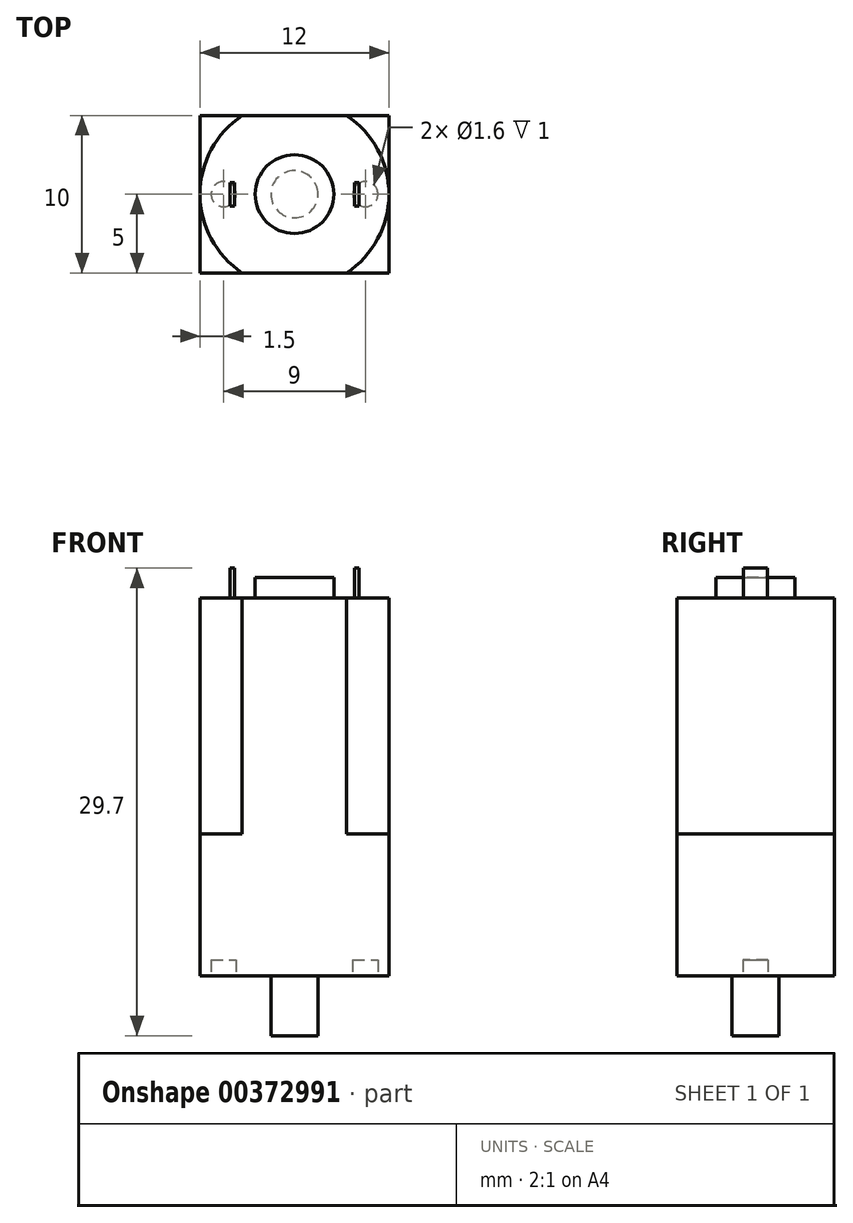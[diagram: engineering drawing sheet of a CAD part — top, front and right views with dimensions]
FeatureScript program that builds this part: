
annotation { "Feature Type Name" : "Feature", "Feature Type Description" : "" }
export const myFeature = defineFeature(function(context is Context, id is Id, definition is map)
    precondition{}
    {
        {
            var Q0;
            Q0=qCreatedBy(makeId("Top.planeOp"),FACE);
            var sketch = newSketch(context, id + "F0", { "sketchPlane" : qUnion([Q0])});
            skArc(sketch, "E0", {"start": v(-3.32, 5) * mm, "mid": v(-6, 0) * mm, "end": v(-3.32, -5) * mm});
            skLineSegment(sketch, "E1", {"start": v(-6, 0) * mm, "end": v(6, 0) * mm, "construction": true});
            skLineSegment(sketch, "E2", {"start": v(-3.32, 5) * mm, "end": v(3.32, 5) * mm});
            skLineSegment(sketch, "E3", {"start": v(-3.32, -5) * mm, "end": v(3.32, -5) * mm});
            skArc(sketch, "E4.trimOffspring", {"start": v(3.32, -5) * mm, "mid": v(6, 0) * mm, "end": v(3.32, 5) * mm});
            skSolve(sketch);
        }
        {
            var Q0;
            Q0 = qSketchRegion(id + "F0", true);
            extrude(context, id + "F1", {"entities" : qUnion([Q0]), "depth" : 15 * mm});
        }
        {
            var Q0;
            Q0=makeQuery(id+"F1.opExtrude","CAP_FACE",FACE,{"disambiguationData":[OSD([sQuery(id+"F0.wireOp",EDGE,"E0"),sQuery(id+"F0.wireOp",EDGE,"E2"),sQuery(id+"F0.wireOp",EDGE,"E3"),sQuery(id+"F0.wireOp",EDGE,"E4.trimOffspring")])],"isStart":true});
            var sketch = newSketch(context, id + "F2", { "sketchPlane" : qUnion([Q0])});
            skLineSegment(sketch, "E5.bottom", {"start": v(-6, 5) * mm, "end": v(6, 5) * mm});
            skLineSegment(sketch, "E5.top", {"start": v(-6, -5) * mm, "end": v(6, -5) * mm});
            skLineSegment(sketch, "E5.left", {"start": v(-6, 5) * mm, "end": v(-6, -5) * mm});
            skLineSegment(sketch, "E5.right", {"start": v(6, 5) * mm, "end": v(6, -5) * mm});
            skPoint(sketch, "E5.middle", {"position": v(0, 0) * mm});
            skSolve(sketch);
        }
        {
            var Q0;
            Q0 = qSketchRegion(id + "F2", true);
            extrude(context, id + "F3", {"entities" : qUnion([Q0]), "operationType" : NewBodyOperationType.ADD, "depth" : 9 * mm});
        }
        {
            var Q0;
            Q0=makeQuery(id+"F3.opExtrude","CAP_FACE",FACE,{"disambiguationData":[OSD([sQuery(id+"F2.wireOp",EDGE,"E5.bottom"),sQuery(id+"F2.wireOp",EDGE,"E5.top"),sQuery(id+"F2.wireOp",EDGE,"E5.left"),sQuery(id+"F2.wireOp",EDGE,"E5.right")])],"isStart":false});
            var sketch = newSketch(context, id + "F4", { "sketchPlane" : qUnion([Q0])});
            skCircle(sketch, "E6", {"center": v(-4.5, 0) * mm, "radius": 0.8 * mm});
            skLineSegment(sketch, "E7", {"start": v(0, 0) * mm, "end": v(0, 8.29) * mm, "construction": true});
            skCircle(sketch, "E8", {"center": v(4.5, 0) * mm, "radius": 0.8 * mm});
            skSolve(sketch);
        }
        {
            var Q0;
            Q0 = qSketchRegion(id + "F4", true);
            extrude(context, id + "F5", {"entities" : qUnion([Q0]), "operationType" : NewBodyOperationType.REMOVE, "oppositeDirection" : true, "depth" : 1 * mm});
        }
        {
            var Q0;
            Q0=makeQuery(id+"F3.opExtrude","CAP_FACE",FACE,{"disambiguationData":[OSD([sQuery(id+"F2.wireOp",EDGE,"E5.bottom"),sQuery(id+"F2.wireOp",EDGE,"E5.top"),sQuery(id+"F2.wireOp",EDGE,"E5.left"),sQuery(id+"F2.wireOp",EDGE,"E5.right")])],"isStart":false});
            var sketch = newSketch(context, id + "F6", { "sketchPlane" : qUnion([Q0])});
            skCircle(sketch, "E9", {"center": v(0, 0) * mm, "radius": 1.5 * mm});
            skSolve(sketch);
        }
        {
            var Q0;
            Q0 = qSketchRegion(id + "F6", true);
            extrude(context, id + "F7", {"entities" : qUnion([Q0]), "operationType" : NewBodyOperationType.ADD, "depth" : 3.8 * mm});
        }
        {
            var Q0;
            Q0=makeQuery(id+"F1.opExtrude","CAP_FACE",FACE,{"disambiguationData":[OSD([sQuery(id+"F0.wireOp",EDGE,"E0"),sQuery(id+"F0.wireOp",EDGE,"E2"),sQuery(id+"F0.wireOp",EDGE,"E3"),sQuery(id+"F0.wireOp",EDGE,"E4.trimOffspring")])],"isStart":false});
            var sketch = newSketch(context, id + "F8", { "sketchPlane" : qUnion([Q0])});
            skCircle(sketch, "E10", {"center": v(0, 0) * mm, "radius": 2.5 * mm});
            skSolve(sketch);
        }
        {
            var Q0;
            Q0 = qSketchRegion(id + "F8", true);
            extrude(context, id + "F9", {"entities" : qUnion([Q0]), "operationType" : NewBodyOperationType.ADD, "depth" : 1.3 * mm});
        }
        {
            var Q0;
            Q0=makeQuery(id+"F1.opExtrude","CAP_FACE",FACE,{"disambiguationData":[OSD([sQuery(id+"F0.wireOp",EDGE,"E0"),sQuery(id+"F0.wireOp",EDGE,"E2"),sQuery(id+"F0.wireOp",EDGE,"E3"),sQuery(id+"F0.wireOp",EDGE,"E4.trimOffspring")])],"isStart":false});
            var sketch = newSketch(context, id + "F10", { "sketchPlane" : qUnion([Q0])});
            skLineSegment(sketch, "E11.bottom", {"start": v(3.8, 0.75) * mm, "end": v(4.1, 0.75) * mm});
            skLineSegment(sketch, "E11.top", {"start": v(3.8, -0.75) * mm, "end": v(4.1, -0.75) * mm});
            skLineSegment(sketch, "E11.left", {"start": v(3.8, 0.75) * mm, "end": v(3.8, -0.75) * mm});
            skLineSegment(sketch, "E11.right", {"start": v(4.1, 0.75) * mm, "end": v(4.1, -0.75) * mm});
            skLineSegment(sketch, "E12", {"start": v(3.8, 0) * mm, "end": v(0, 0) * mm, "construction": true});
            skLineSegment(sketch, "E13", {"start": v(0, 0) * mm, "end": v(0, 4.2) * mm, "construction": true});
            skLineSegment(sketch, "E14.MirrorCS", {"start": v(-3.8, -0.75) * mm, "end": v(-4.1, -0.75) * mm});
            skLineSegment(sketch, "E15.MirrorCS", {"start": v(-3.8, 0.75) * mm, "end": v(-4.1, 0.75) * mm});
            skLineSegment(sketch, "E16.MirrorCS", {"start": v(-4.1, 0.75) * mm, "end": v(-4.1, -0.75) * mm});
            skLineSegment(sketch, "E17.MirrorCS", {"start": v(-3.8, 0.75) * mm, "end": v(-3.8, -0.75) * mm});
            skSolve(sketch);
        }
        {
            var Q0;
            Q0 = qSketchRegion(id + "F10", true);
            extrude(context, id + "F11", {"entities" : qUnion([Q0]), "operationType" : NewBodyOperationType.ADD, "depth" : 1.9 * mm});
        }
    });
